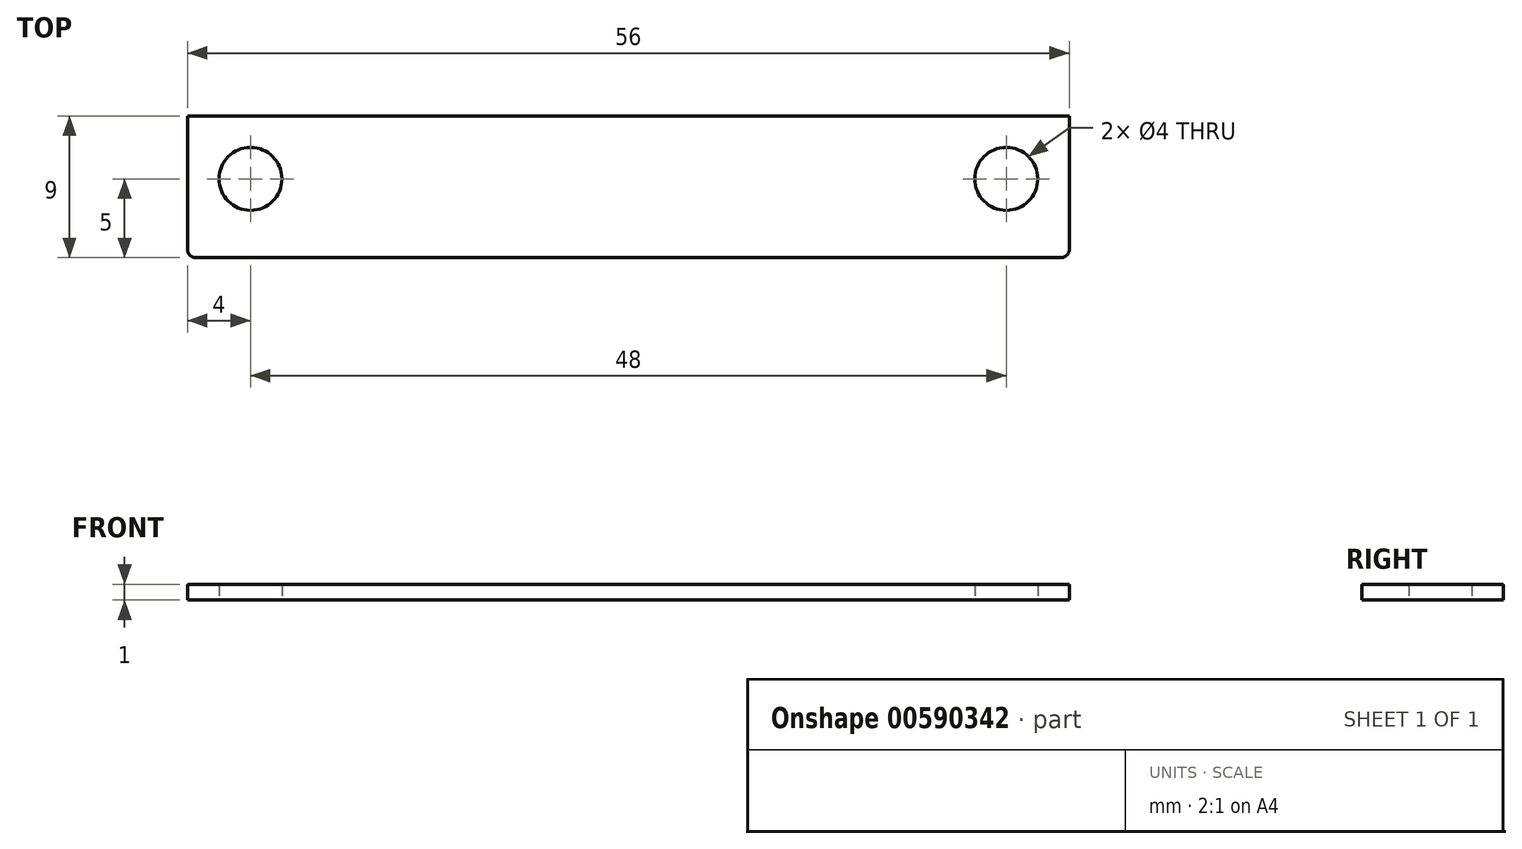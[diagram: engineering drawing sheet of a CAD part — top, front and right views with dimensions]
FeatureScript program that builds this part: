
annotation { "Feature Type Name" : "Feature", "Feature Type Description" : "" }
export const myFeature = defineFeature(function(context is Context, id is Id, definition is map)
    precondition{}
    {
        {
            var Q0;
            Q0=qCreatedBy(makeId("Top.planeOp"),FACE);
            var sketch = newSketch(context, id + "F0", { "sketchPlane" : qUnion([Q0])});
            skLineSegment(sketch, "E0.bottom", {"start": v(-27.5, -5) * mm, "end": v(27.5, -5) * mm});
            skLineSegment(sketch, "E0.left", {"start": v(-28, -4.5) * mm, "end": v(-28, 4) * mm});
            skLineSegment(sketch, "E0.right", {"start": v(28, -4.5) * mm, "end": v(28, 4) * mm});
            skPoint(sketch, "E0.middle", {"position": v(0, 0) * mm});
            skPoint(sketch, "E1.visualSharp", {"position": v(-28, 5) * mm});
            skPoint(sketch, "E2.visualSharp", {"position": v(-28, -5) * mm});
            skArc(sketch, "E2.filletArc", {"start": v(-28, -4.5) * mm, "mid": v(-27.85, -4.85) * mm, "end": v(-27.5, -5) * mm});
            skPoint(sketch, "E3.visualSharp", {"position": v(28, 5) * mm});
            skPoint(sketch, "E4.visualSharp", {"position": v(28, -5) * mm});
            skArc(sketch, "E4.filletArc", {"start": v(27.5, -5) * mm, "mid": v(27.85, -4.85) * mm, "end": v(28, -4.5) * mm});
            skCircle(sketch, "E5", {"center": v(-24, 0) * mm, "radius": 2 * mm});
            skCircle(sketch, "E6", {"center": v(24, 0) * mm, "radius": 2 * mm});
            skLineSegment(sketch, "E7.0", {"start": v(-28, 4) * mm, "end": v(28, 4) * mm});
            skSolve(sketch);
        }
        {
            var Q0;
            Q0 = qSketchRegion(id + "F0", true);
            extrude(context, id + "F1", {"entities" : qUnion([Q0]), "depth" : 1 * mm, "offsetDistance" : 25 * mm});
        }
    });
